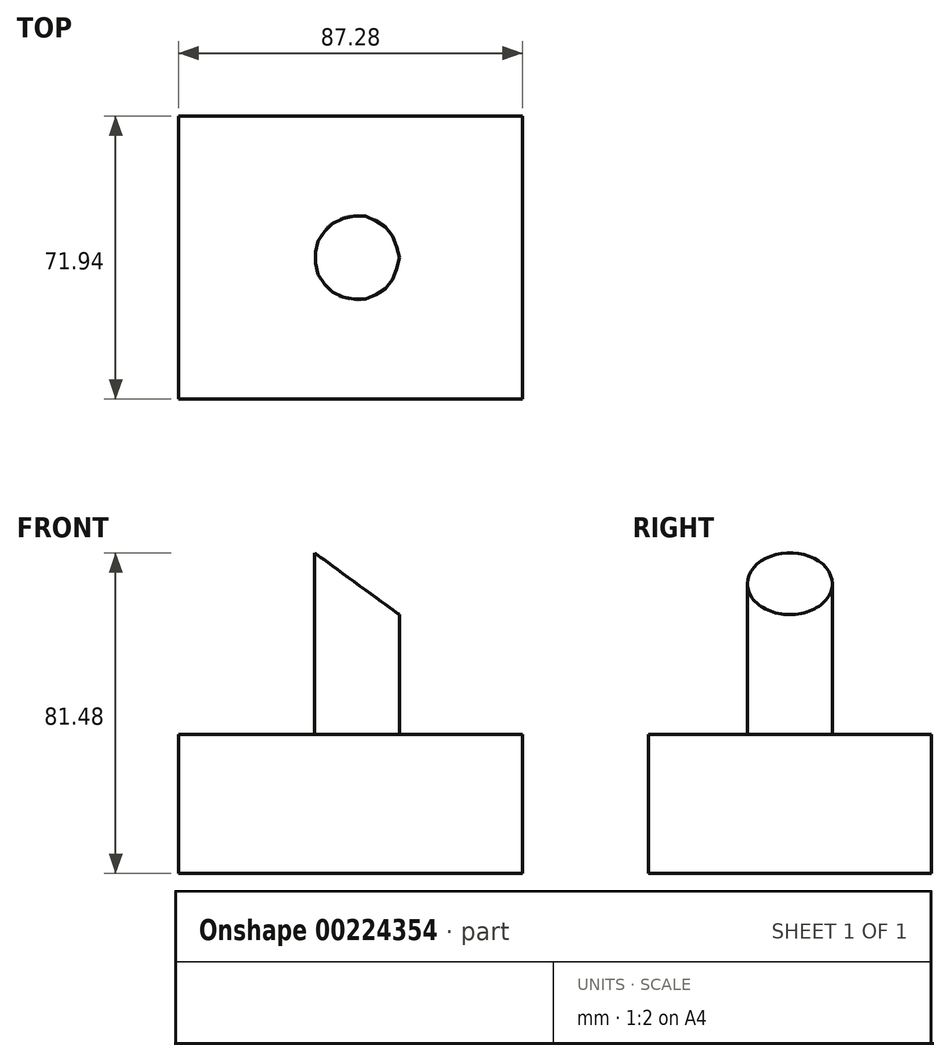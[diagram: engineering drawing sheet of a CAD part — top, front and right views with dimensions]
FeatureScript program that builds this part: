
annotation { "Feature Type Name" : "Feature", "Feature Type Description" : "" }
export const myFeature = defineFeature(function(context is Context, id is Id, definition is map)
    precondition{}
    {
        {
            var Q0;
            Q0=qCreatedBy(makeId("Top.planeOp"),FACE);
            var sketch = newSketch(context, id + "F0", { "sketchPlane" : qUnion([Q0])});
            skLineSegment(sketch, "E0.bottom", {"start": v(43.64, -35.97) * mm, "end": v(-43.64, -35.97) * mm});
            skLineSegment(sketch, "E0.top", {"start": v(43.64, 35.97) * mm, "end": v(-43.64, 35.97) * mm});
            skLineSegment(sketch, "E0.left", {"start": v(43.64, -35.97) * mm, "end": v(43.64, 35.97) * mm});
            skLineSegment(sketch, "E0.right", {"start": v(-43.64, -35.97) * mm, "end": v(-43.64, 35.97) * mm});
            skPoint(sketch, "E0.middle", {"position": v(0, 0) * mm});
            skCircle(sketch, "E1", {"center": v(1.6, 0) * mm, "radius": 10.8 * mm});
            skSolve(sketch);
        }
        {
            var Q0;
            Q0=makeQuery(id+"F0.imprint","IMPRINT",FACE,{"disambiguationData":[TD([[makeQuery(id+"F0.imprint","IMPRINT",EDGE,{"derivedFrom":sQuery(id+"F0.wireOp",EDGE,"E1")}),1.0]])]});
            extrude(context, id + "F1", {"entities" : qUnion([Q0]), "depth" : 86.61 * mm});
        }
        {
            var Q0;
            Q0=makeQuery(id+"F0.imprint","IMPRINT",FACE,{"disambiguationData":[TD([[makeQuery(id+"F0.imprint","IMPRINT",EDGE,{"derivedFrom":sQuery(id+"F0.wireOp",EDGE,"E0.bottom")}),-1.0]])]});
            extrude(context, id + "F2", {"entities" : qUnion([Q0]), "operationType" : NewBodyOperationType.ADD, "depth" : 35.3 * mm});
        }
        {
            var Q0;
            Q0=qCreatedBy(makeId("Front.planeOp"),FACE);
            var sketch = newSketch(context, id + "F3", { "sketchPlane" : qUnion([Q0])});
            skLineSegment(sketch, "E2", {"start": v(-31.5, 97.7) * mm, "end": v(33.42, 50.45) * mm});
            skLineSegment(sketch, "E3", {"start": v(33.42, 50.45) * mm, "end": v(33.42, 102.4) * mm});
            skLineSegment(sketch, "E4", {"start": v(33.42, 102.4) * mm, "end": v(-31.5, 97.7) * mm});
            skSolve(sketch);
        }
        {
            var Q0;
            Q0 = qSketchRegion(id + "F3", true);
            extrude(context, id + "F4", {"entities" : qUnion([Q0]), "operationType" : NewBodyOperationType.REMOVE, "oppositeDirection" : true, "depth" : 25.4 * mm, "hasSecondDirection" : true, "secondDirectionOppositeDirection" : false, "secondDirectionDepth" : 25.4 * mm});
        }
    });
